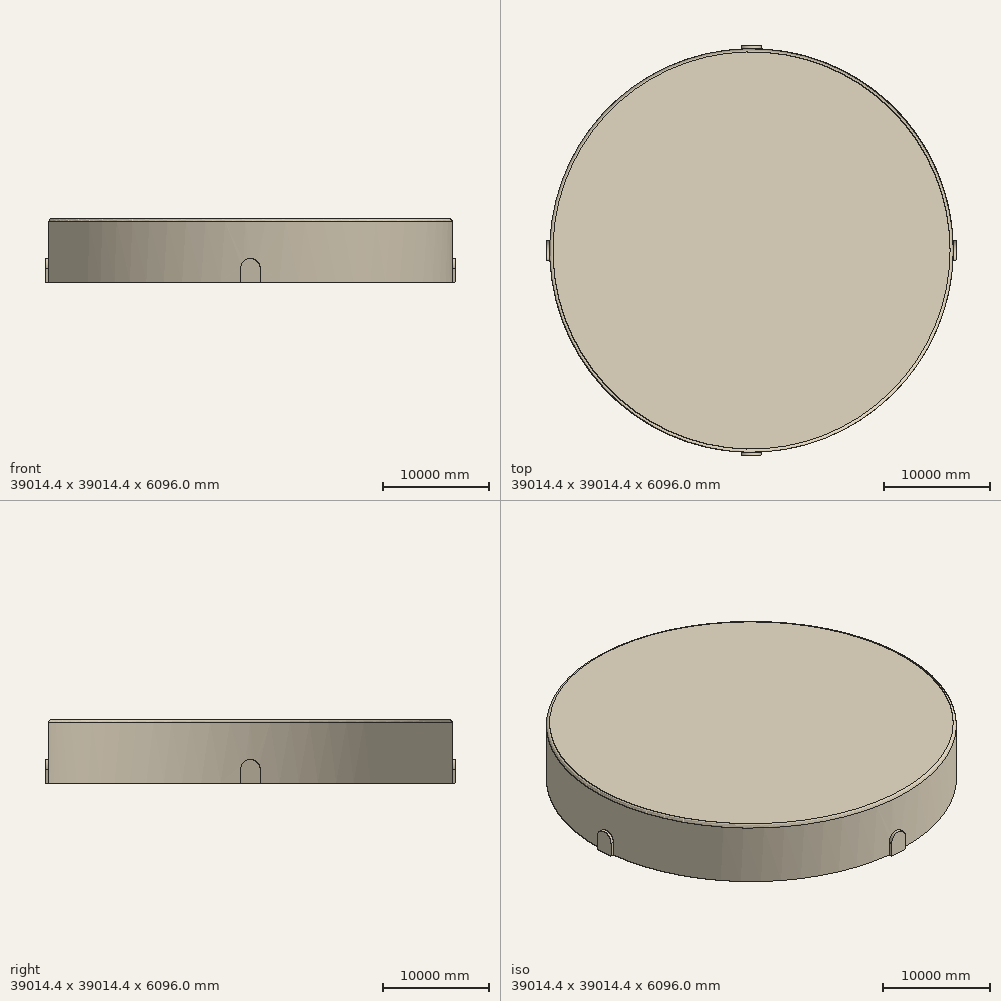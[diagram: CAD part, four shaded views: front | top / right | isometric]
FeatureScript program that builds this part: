
annotation { "Feature Type Name" : "Feature", "Feature Type Description" : "" }
export const myFeature = defineFeature(function(context is Context, id is Id, definition is map)
    precondition{}
    {
        {
            var Q0;
            Q0=qCreatedBy(makeId("Top.planeOp"),FACE);
            var sketch = newSketch(context, id + "F0", { "sketchPlane" : qUnion([Q0])});
            skCircle(sketch, "E0", {"center": v(0, 0) * mm, "radius": 19202.4 * mm});
            skSolve(sketch);
        }
        {
            var Q0;
            Q0 = qSketchRegion(id + "F0", true);
            extrude(context, id + "F1", {"entities" : qUnion([Q0]), "depth" : 6096 * mm});
        }
        {
            var Q0;
            Q0=qCreatedBy(makeId("Front.planeOp"),FACE);
            var sketch = newSketch(context, id + "F2", { "sketchPlane" : qUnion([Q0])});
            skLineSegment(sketch, "E1", {"start": v(0, 0) * mm, "end": v(914.4, 0) * mm});
            skLineSegment(sketch, "E2", {"start": v(0, 0) * mm, "end": v(-914.4, 0) * mm});
            skLineSegment(sketch, "E3", {"start": v(914.4, 0) * mm, "end": v(914.4, 1371.6) * mm});
            skLineSegment(sketch, "E4", {"start": v(-914.4, 0) * mm, "end": v(-914.4, 1371.6) * mm});
            skArc(sketch, "E5", {"start": v(914.4, 1371.6) * mm, "mid": v(0, 2286) * mm, "end": v(-914.4, 1371.6) * mm});
            skSolve(sketch);
        }
        {
            var Q0;
            Q0 = qSketchRegion(id + "F2", true);
            extrude(context, id + "F3", {"entities" : qUnion([Q0]), "operationType" : NewBodyOperationType.ADD, "depth" : 19507.2 * mm, "hasSecondDirection" : true, "secondDirectionOppositeDirection" : true, "secondDirectionDepth" : 19507.2 * mm});
        }
        {
            var Q0;
            Q0=qCreatedBy(makeId("Right.planeOp"),FACE);
            var sketch = newSketch(context, id + "F4", { "sketchPlane" : qUnion([Q0])});
            skLineSegment(sketch, "E6", {"start": v(0, 0) * mm, "end": v(914.4, 0) * mm});
            skLineSegment(sketch, "E7", {"start": v(0, 0) * mm, "end": v(-914.4, 0) * mm});
            skLineSegment(sketch, "E8", {"start": v(914.4, 0) * mm, "end": v(914.4, 1371.6) * mm});
            skLineSegment(sketch, "E9", {"start": v(-914.4, 0) * mm, "end": v(-914.4, 1371.6) * mm});
            skArc(sketch, "E10", {"start": v(914.4, 1371.6) * mm, "mid": v(0, 2286) * mm, "end": v(-914.4, 1371.6) * mm});
            skSolve(sketch);
        }
        {
            var Q0;
            Q0 = qSketchRegion(id + "F4", true);
            extrude(context, id + "F5", {"entities" : qUnion([Q0]), "operationType" : NewBodyOperationType.ADD, "depth" : 19507.2 * mm, "hasSecondDirection" : true, "secondDirectionOppositeDirection" : true, "secondDirectionDepth" : 19507.2 * mm});
        }
        {
            var Q0;
            Q0=makeQuery(id+"F1.opExtrude","CAP_EDGE",EDGE,{"disambiguationData":[OSD([sQuery(id+"F0.wireOp",EDGE,"E0")])],"isStart":false});
            fillet(context, id + "F6", {"entities" : qUnion([Q0]), "radius" : 304.8 * mm, "tangentPropagation" : true, "allowEdgeOverflow" : false});
        }
    });
